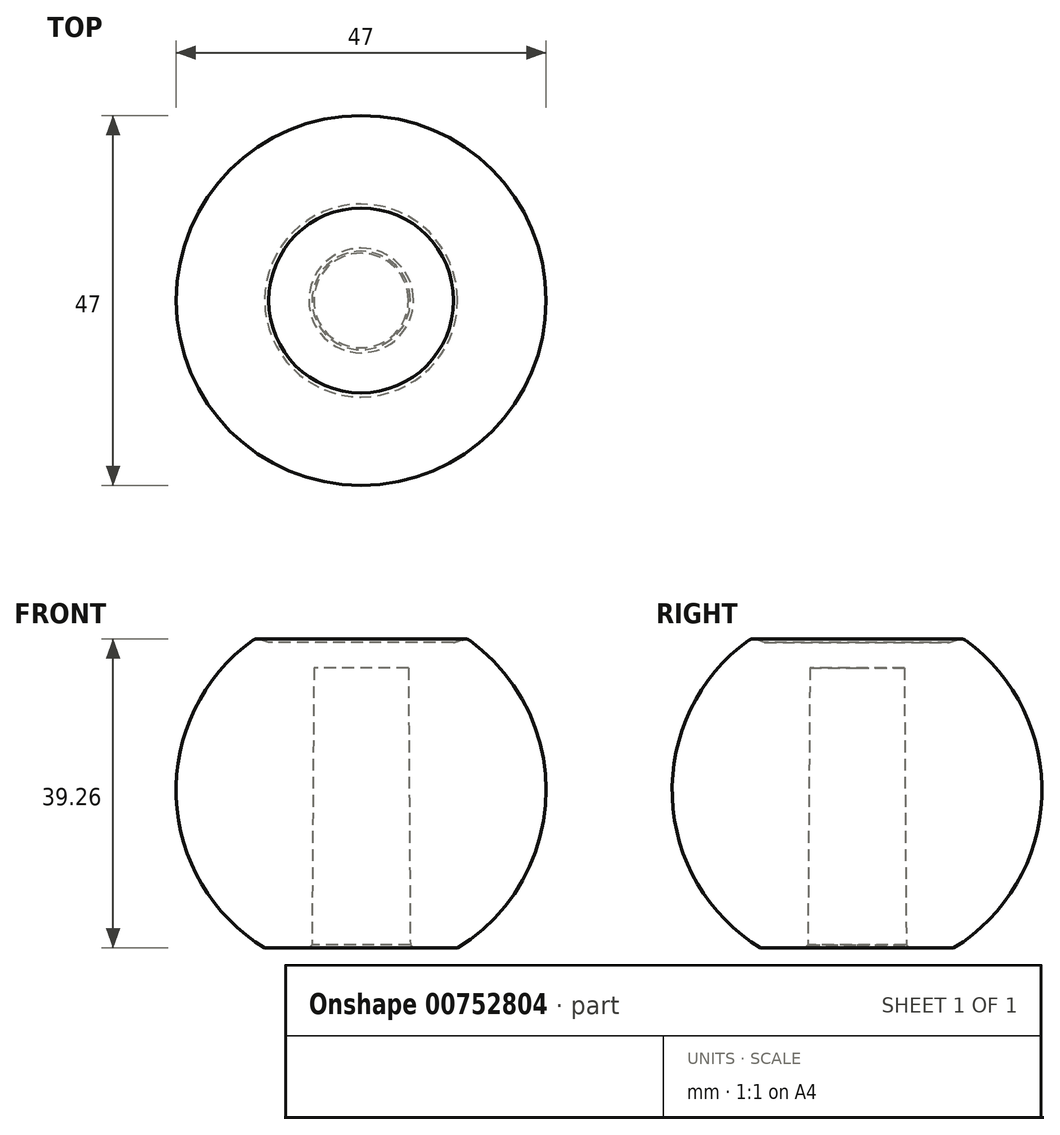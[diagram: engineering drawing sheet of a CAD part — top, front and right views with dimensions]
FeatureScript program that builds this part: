
annotation { "Feature Type Name" : "Feature", "Feature Type Description" : "" }
export const myFeature = defineFeature(function(context is Context, id is Id, definition is map)
    precondition{}
    {
        {
            var Q0;
            Q0=qCreatedBy(makeId("Front.planeOp"),FACE);
            var sketch = newSketch(context, id + "F0", { "sketchPlane" : qUnion([Q0])});
            skLineSegment(sketch, "E0", {"start": v(6, 15.5) * mm, "end": v(6.25, -20.05) * mm});
            skArc(sketch, "E1", {"start": v(12.25, -20.05) * mm, "mid": v(22.62, 6.36) * mm, "end": v(0, 23.5) * mm});
            skLineSegment(sketch, "E2", {"start": v(0, 23.5) * mm, "end": v(0, 15.5) * mm});
            skLineSegment(sketch, "E3", {"start": v(0, 15.5) * mm, "end": v(6, 15.5) * mm});
            skLineSegment(sketch, "E4", {"start": v(0, 23.5) * mm, "end": v(-14.34, 23.5) * mm, "construction": true});
            skLineSegment(sketch, "E5", {"start": v(6.25, -20.05) * mm, "end": v(12.25, -20.05) * mm});
            skLineSegment(sketch, "E6", {"start": v(0, -25.4) * mm, "end": v(0, 58.05) * mm, "construction": true});
            skLineSegment(sketch, "E7", {"start": v(0, 18.74) * mm, "end": v(11.74, 18.74) * mm});
            skLineSegment(sketch, "E8", {"start": v(11.74, 18.74) * mm, "end": v(13.37, 19.33) * mm});
            skSolve(sketch);
        }
        {
            var Q0;
            Q0=makeQuery(id+"F0.imprint","IMPRINT",FACE,{"disambiguationData":[TD([[makeQuery(id+"F0.imprint","IMPRINT",EDGE,{"derivedFrom":sQuery(id+"F0.wireOp",EDGE,"E0")}),1.0]])]});
            var Q1;
            Q1=sQuery(id+"F0.wireOp",EDGE,"E2");
            revolve(context, id + "F1", {"surfaceOperationType" : NewSurfaceOperationType.NEW, "entities" : qUnion([Q0]), "axis" : qUnion([Q1]), "revolveType" : RevolveType.FULL});
        }
        {
            var Q0;
            Q0=makeQuery(id+"F1.opRevolve","SWEPT_EDGE",EDGE,{"disambiguationData":[OSD([sQuery(id+"F0.wireOp",EDGE,"E1"),sQuery(id+"F0.wireOp",EDGE,"E8")])]});
            fillet(context, id + "F2", {"entities" : qUnion([Q0]), "tangentPropagation" : true, "radius" : 1 * mm, "defaultsChanged" : true, "vertexSettings" : [], "allowEdgeOverflow" : false});
        }
        {
            var Q0;
            Q0=makeQuery(id+"F1.opRevolve","SWEPT_EDGE",EDGE,{"disambiguationData":[OSD([sQuery(id+"F0.wireOp",EDGE,"E0"),sQuery(id+"F0.wireOp",EDGE,"E5")])]});
            chamfer(context, id + "F3", {"entities" : qUnion([Q0]), "width" : 0.4 * mm, "tangentPropagation" : true});
        }
    });
